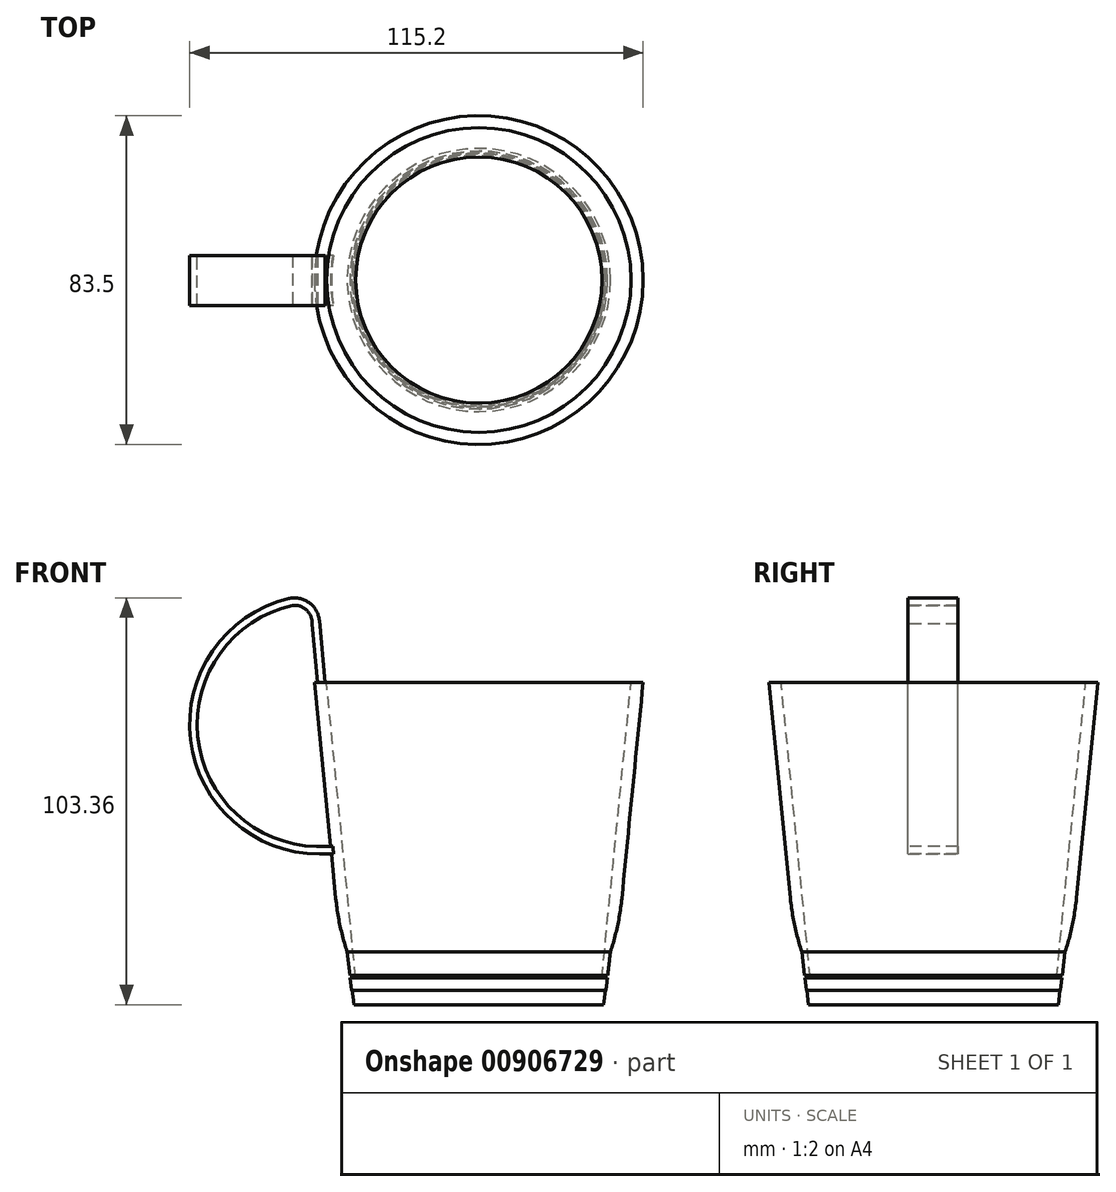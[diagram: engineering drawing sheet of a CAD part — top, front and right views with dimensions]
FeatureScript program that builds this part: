
annotation { "Feature Type Name" : "Feature", "Feature Type Description" : "" }
export const myFeature = defineFeature(function(context is Context, id is Id, definition is map)
    precondition{}
    {
        {
            var Q0;
            Q0=qCreatedBy(makeId("Top.planeOp"),FACE);
            var sketch = newSketch(context, id + "F0", { "sketchPlane" : qUnion([Q0])});
            skCircle(sketch, "E0", {"center": v(0, 0) * mm, "radius": 33.02 * mm});
            skSolve(sketch);
        }
        {
            var Q0;
            Q0=makeQuery(id+"F0.imprint","IMPRINT",FACE,{"disambiguationData":[TD([[makeQuery(id+"F0.imprint","IMPRINT",EDGE,{"derivedFrom":sQuery(id+"F0.wireOp",EDGE,"E0")}),1.0]])]});
            extrude(context, id + "F1", {"entities" : qUnion([Q0]), "depth" : 78.23 * mm, "offsetDistance" : 25.4 * mm, "hasDraft" : true, "draftAngle" : 5.63 * degree});
        }
        {
            var Q0;
            Q0=qCreatedBy(makeId("Front.planeOp"),FACE);
            var sketch = newSketch(context, id + "F2", { "sketchPlane" : qUnion([Q0])});
            skLineSegment(sketch, "E1", {"start": v(0, 0) * mm, "end": v(-32.15, 0) * mm});
            skLineSegment(sketch, "E2", {"start": v(-31.7, -3.63) * mm, "end": v(0, -3.63) * mm});
            skLineSegment(sketch, "E3", {"start": v(0, -3.63) * mm, "end": v(0, 0) * mm});
            skLineSegment(sketch, "E4", {"start": v(-32.15, 0) * mm, "end": v(-31.7, -3.63) * mm});
            skSolve(sketch);
        }
        {
            var Q0;
            Q0=makeQuery(id+"F1.opExtrude","CAP_FACE",FACE,{"disambiguationData":[OSD([sQuery(id+"F0.wireOp",EDGE,"E0")])],"isStart":true});
            var sketch = newSketch(context, id + "F3", { "sketchPlane" : qUnion([Q0])});
            skCircle(sketch, "E5", {"center": v(0, 0) * mm, "radius": 34.04 * mm});
            skSolve(sketch);
        }
        {
            var Q0;
            Q0=makeQuery(id+"F3.imprint","IMPRINT",FACE,{"disambiguationData":[TD([[makeQuery(id+"F3.imprint","IMPRINT",EDGE,{"derivedFrom":sQuery(id+"F3.wireOp",EDGE,"E5")}),1.0]])]});
            extrude(context, id + "F4", {"entities" : qUnion([Q0]), "operationType" : NewBodyOperationType.ADD, "oppositeDirection" : true, "depth" : 78.23 * mm, "offsetDistance" : 25.4 * mm, "hasDraft" : true, "draftAngle" : 5.63 * degree});
        }
        {
            var Q0;
            {var subQ0=sQuery(id+"F0.wireOp",EDGE,"E0");Q0=makeQuery(id+"F4.boolean.opBoolean","MERGE",FACE,{"derivedFrom":[makeQuery(id+"F1.opExtrude","CAP_FACE",FACE,{"disambiguationData":[OSD([subQ0])],"isStart":false}),makeQuery(id+"F4.opExtrude","CAP_FACE",FACE,{"disambiguationData":[OSD([subQ0,sQuery(id+"F3.wireOp",EDGE,"E5")])],"isStart":false})]});}
            shell(context, id + "F5", {"entities" : qUnion([Q0]), "thickness" : 3.05 * mm});
        }
        {
            var Q0;
            Q0=qCreatedBy(makeId("Front.planeOp"),FACE);
            var sketch = newSketch(context, id + "F6", { "sketchPlane" : qUnion([Q0])});
            skLineSegment(sketch, "E6", {"start": v(32.31, 0) * mm, "end": v(32.68, 3.23) * mm});
            skLineSegment(sketch, "E7", {"start": v(44.09, 0) * mm, "end": v(32.31, 0) * mm});
            skLineSegment(sketch, "E8", {"start": v(0, 0) * mm, "end": v(0, 77.76) * mm});
            skLineSegment(sketch, "E9", {"start": v(44.09, 54.35) * mm, "end": v(39.45, 54.35) * mm});
            skLineSegment(sketch, "E10", {"start": v(39.45, 54.35) * mm, "end": v(39.39, 54.24) * mm});
            skLineSegment(sketch, "E11", {"start": v(44.09, 54.35) * mm, "end": v(44.09, 0) * mm});
            skPoint(sketch, "E12.orphan", {"position": v(50.5, 0) * mm});
            skLineSegment(sketch, "E13", {"start": v(41.76, 78.23) * mm, "end": v(36.36, 23.6) * mm});
            skArc(sketch, "E14", {"start": v(33.44, 9.8) * mm, "mid": v(35.28, 16.62) * mm, "end": v(36.36, 23.6) * mm});
            skLineSegment(sketch, "E15.trimOffspring", {"start": v(32.79, 4.1) * mm, "end": v(33.44, 9.8) * mm});
            skLineSegment(sketch, "E16.bottom", {"start": v(32.09, 3.86) * mm, "end": v(32.76, 3.86) * mm});
            skLineSegment(sketch, "E16.top", {"start": v(32, 3.23) * mm, "end": v(32.68, 3.23) * mm});
            skLineSegment(sketch, "E17.trimOffspring", {"start": v(32.76, 3.86) * mm, "end": v(32.84, 4.56) * mm});
            skLineSegment(sketch, "E18", {"start": v(32.09, 3.86) * mm, "end": v(32, 3.23) * mm});
            skSolve(sketch);
        }
        {
            var Q0;
            Q0=makeQuery(id+"F6.imprint","IMPRINT",FACE,{"disambiguationData":[TD([[makeQuery(id+"F6.imprint","IMPRINT",EDGE,{"derivedFrom":sQuery(id+"F6.wireOp",EDGE,"E6")}),-1.0]])]});
            var Q1;
            Q1=sQuery(id+"F6.wireOp",EDGE,"E8");
            revolve(context, id + "F7", {"operationType" : NewBodyOperationType.REMOVE, "surfaceOperationType" : NewSurfaceOperationType.NEW, "entities" : qUnion([Q0]), "axis" : qUnion([Q1]), "revolveType" : RevolveType.FULL, "oppositeDirection" : true});
        }
        {
            var Q0;
            Q0=qCreatedBy(makeId("Front.planeOp"),FACE);
            var sketch = newSketch(context, id + "F8", { "sketchPlane" : qUnion([Q0])});
            skLineSegment(sketch, "E19", {"start": v(-38.71, 73.9) * mm, "end": v(-40.53, 93.92) * mm});
            skLineSegment(sketch, "E20", {"start": v(-40.53, 34.68) * mm, "end": v(-35.06, 34.68) * mm});
            skArc(sketch, "E21.filletArc", {"start": v(-40.53, 93.92) * mm, "mid": v(-43.17, 98.52) * mm, "end": v(-48.37, 99.52) * mm});
            skArc(sketch, "E22", {"start": v(-48.37, 99.52) * mm, "mid": v(-73.18, 63.62) * mm, "end": v(-40.53, 34.68) * mm});
            skSolve(sketch);
        }
        {
            var Q0;
            {var subQ0=sQuery(id+"F0.wireOp",EDGE,"E0");Q0=makeQuery(id+"F4.boolean.opBoolean","MERGE",FACE,{"derivedFrom":[makeQuery(id+"F1.opExtrude","CAP_FACE",FACE,{"disambiguationData":[OSD([subQ0])],"isStart":false}),makeQuery(id+"F4.opExtrude","CAP_FACE",FACE,{"disambiguationData":[OSD([subQ0,sQuery(id+"F3.wireOp",EDGE,"E5")])],"isStart":false})]});}
            var sketch = newSketch(context, id + "F9", { "sketchPlane" : qUnion([Q0])});
            skLineSegment(sketch, "E23.bottom", {"start": v(-71.68, 6.2) * mm, "end": v(-69.64, 6.2) * mm});
            skLineSegment(sketch, "E23.top", {"start": v(-71.68, -6.5) * mm, "end": v(-69.64, -6.5) * mm});
            skLineSegment(sketch, "E23.left", {"start": v(-71.68, 6.2) * mm, "end": v(-71.68, -6.5) * mm});
            skLineSegment(sketch, "E23.right", {"start": v(-69.64, 6.2) * mm, "end": v(-69.64, -6.5) * mm});
            skSolve(sketch);
        }
        {
            var Q0;
            Q0=makeQuery(id+"F2.imprint","IMPRINT",FACE,{"disambiguationData":[TD([[makeQuery(id+"F2.imprint","IMPRINT",EDGE,{"derivedFrom":sQuery(id+"F2.wireOp",EDGE,"E1")}),1.0]])]});
            var Q1;
            Q1=sQuery(id+"F2.wireOp",EDGE,"E3");
            revolve(context, id + "F10", {"operationType" : NewBodyOperationType.ADD, "surfaceOperationType" : NewSurfaceOperationType.NEW, "entities" : qUnion([Q0]), "axis" : qUnion([Q1]), "revolveType" : RevolveType.FULL});
        }
        {
            var Q0;
            Q0=makeQuery(id+"F9.imprint","IMPRINT",FACE,{"disambiguationData":[TD([[makeQuery(id+"F9.imprint","IMPRINT",EDGE,{"derivedFrom":sQuery(id+"F9.wireOp",EDGE,"E23.bottom")}),-1.0]])]});
            var Q1;
            Q1=sQuery(id+"F8.wireOp",EDGE,"E22");
            var Q2;
            Q2=sQuery(id+"F8.wireOp",EDGE,"E21.filletArc");
            var Q3;
            Q3=sQuery(id+"F8.wireOp",EDGE,"E19");
            var Q4;
            Q4=sQuery(id+"F8.wireOp",EDGE,"E20");
            sweep(context, id + "F11", {"operationType" : NewBodyOperationType.ADD, "profiles" : qUnion([Q0]), "path" : qUnion([Q1, Q2, Q3, Q4])});
        }
    });
